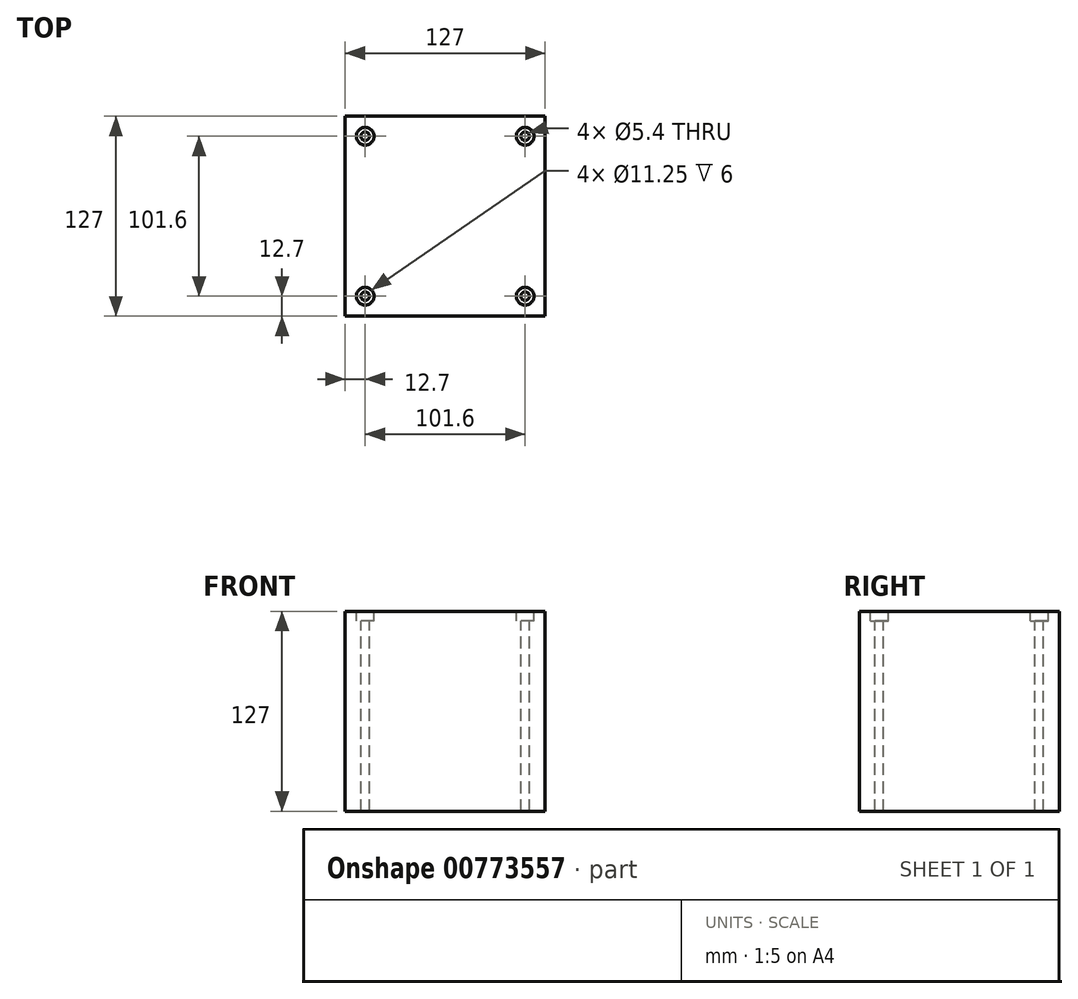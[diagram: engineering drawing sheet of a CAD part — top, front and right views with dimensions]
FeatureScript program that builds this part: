
annotation { "Feature Type Name" : "Feature", "Feature Type Description" : "" }
export const myFeature = defineFeature(function(context is Context, id is Id, definition is map)
    precondition{}
    {
        {
            var Q0;
            Q0=qCreatedBy(makeId("Top.planeOp"),FACE);
            var sketch = newSketch(context, id + "F0", { "sketchPlane" : qUnion([Q0])});
            skLineSegment(sketch, "E0.bottom", {"start": v(63.5, 63.5) * mm, "end": v(-63.5, 63.5) * mm});
            skLineSegment(sketch, "E0.top", {"start": v(63.5, -63.5) * mm, "end": v(-63.5, -63.5) * mm});
            skLineSegment(sketch, "E0.left", {"start": v(63.5, 63.5) * mm, "end": v(63.5, -63.5) * mm});
            skLineSegment(sketch, "E0.right", {"start": v(-63.5, 63.5) * mm, "end": v(-63.5, -63.5) * mm});
            skPoint(sketch, "E0.middle", {"position": v(0, 0) * mm});
            skSolve(sketch);
        }
        {
            var Q0;
            Q0 = qSketchRegion(id + "F0", true);
            extrude(context, id + "F1", {"entities" : qUnion([Q0]), "depth" : -127 * mm, "offsetDistance" : 25.4 * mm});
        }
        {
            var Q0;
            Q0=makeQuery(id+"F1.opExtrude","CAP_FACE",FACE,{"disambiguationData":[OSD([sQuery(id+"F0.wireOp",EDGE,"E0.bottom"),sQuery(id+"F0.wireOp",EDGE,"E0.top"),sQuery(id+"F0.wireOp",EDGE,"E0.left"),sQuery(id+"F0.wireOp",EDGE,"E0.right")])],"isStart":true});
            var sketch = newSketch(context, id + "F2", { "sketchPlane" : qUnion([Q0])});
            skLineSegment(sketch, "E1.bottom", {"start": v(50.8, 50.8) * mm, "end": v(-50.8, 50.8) * mm});
            skLineSegment(sketch, "E1.top", {"start": v(50.8, -50.8) * mm, "end": v(-50.8, -50.8) * mm});
            skLineSegment(sketch, "E1.left", {"start": v(50.8, 50.8) * mm, "end": v(50.8, -50.8) * mm});
            skLineSegment(sketch, "E1.right", {"start": v(-50.8, 50.8) * mm, "end": v(-50.8, -50.8) * mm});
            skPoint(sketch, "E1.middle", {"position": v(0, 0) * mm});
            skSolve(sketch);
        }
        {
            var Q0;
            Q0=sQuery(id+"F2.wireOp",VERTEX,"E1.bottom.end");
            var Q1;
            Q1=sQuery(id+"F2.wireOp",VERTEX,"E1.top.end");
            var Q2;
            Q2=sQuery(id+"F2.wireOp",VERTEX,"E1.top.start");
            var Q3;
            Q3=sQuery(id+"F2.wireOp",VERTEX,"E1.bottom.start");
            var Q4;
            Q4=makeQuery(id+"F1.opExtrude","SWEPT_BODY",BODY,{"disambiguationData":[OSD([sQuery(id+"F0.wireOp",EDGE,"E0.bottom"),sQuery(id+"F0.wireOp",EDGE,"E0.top"),sQuery(id+"F0.wireOp",EDGE,"E0.left"),sQuery(id+"F0.wireOp",EDGE,"E0.right")])]});
            hole(context, id + "F3", {"style" : HoleStyle.C_BORE, "endStyle" : HoleEndStyle.THROUGH, "standardTappedOrClearance" : lookupTablePath({ "standard" : "ISO", "engagement" : "50%", "pitch" : "1 mm", "size" : "M6", "type" : "Tapped" }), "standardBlindInLast" : lookupTablePath({ "standard" : "ISO", "engagement" : "50%", "pitch" : "1 mm", "size" : "M6", "type" : "Tapped" }), "holeDiameter" : 5.4 * mm, "cBoreDiameter" : 11.25 * mm, "cBoreDepth" : 6 * mm, "majorDiameter" : 6 * mm, "showTappedDepth" : true, "tappedDepth" : 20 * mm, "tapClearance" : 3, "locations" : qUnion([Q0, Q1, Q2, Q3]), "scope" : qUnion([Q4])});
        }
    });
